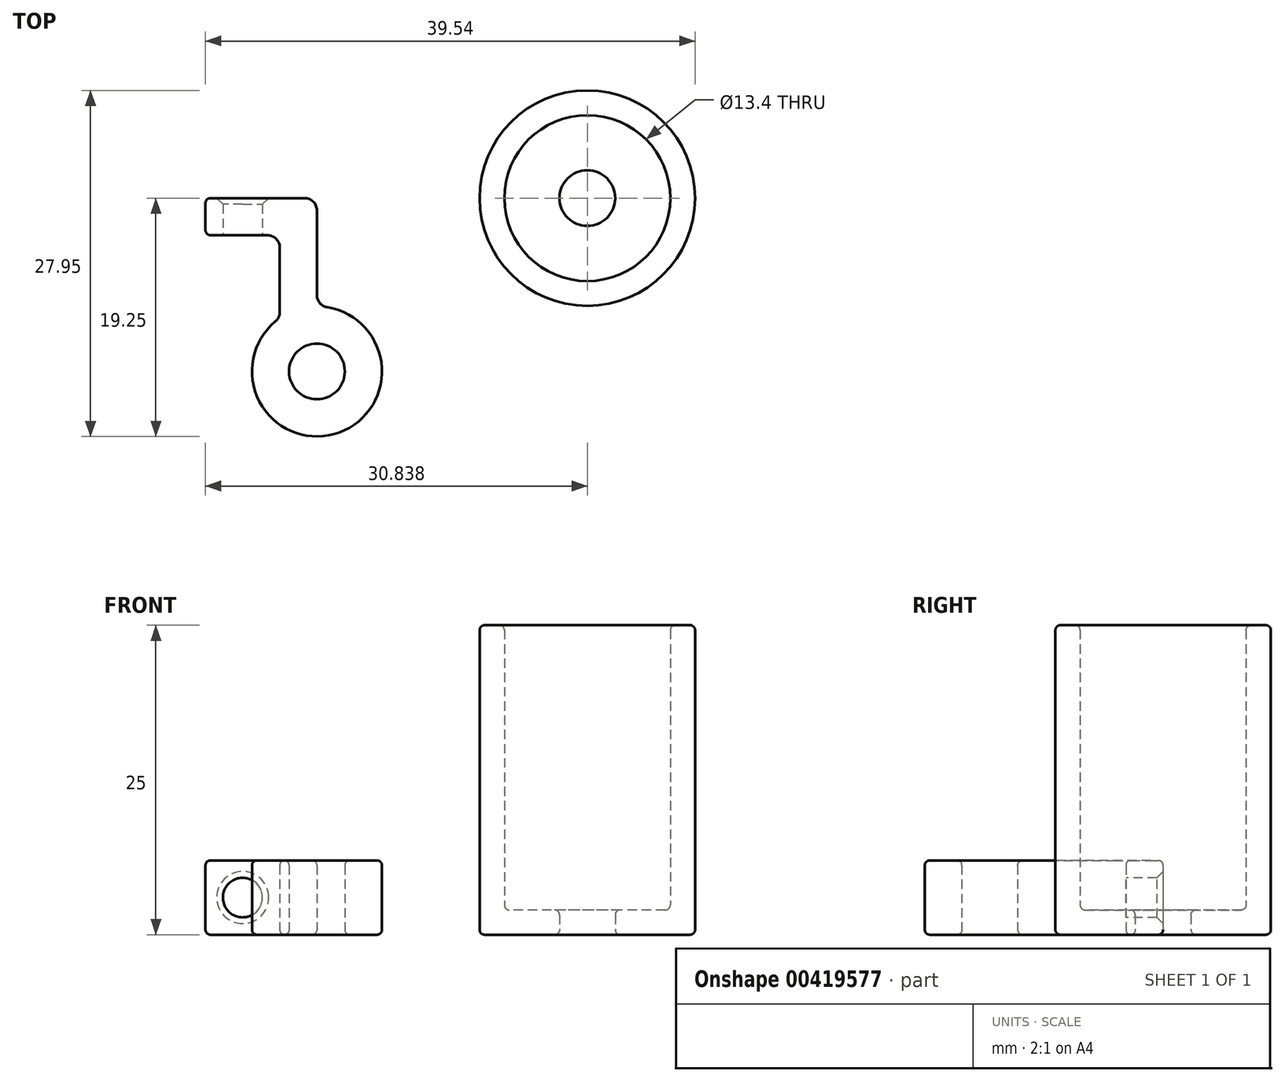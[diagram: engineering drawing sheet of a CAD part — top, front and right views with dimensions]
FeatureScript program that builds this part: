
annotation { "Feature Type Name" : "Feature", "Feature Type Description" : "" }
export const myFeature = defineFeature(function(context is Context, id is Id, definition is map)
    precondition{}
    {
        {
            var Q0;
            Q0=qCreatedBy(makeId("Top.planeOp"),FACE);
            var sketch = newSketch(context, id + "F0", { "sketchPlane" : qUnion([Q0])});
            skLineSegment(sketch, "E0", {"start": v(0, 0) * mm, "end": v(9, 0) * mm});
            skLineSegment(sketch, "E1", {"start": v(9, 0) * mm, "end": v(9, -8.75) * mm});
            skLineSegment(sketch, "E2", {"start": v(9, -14) * mm, "end": v(6, -14) * mm, "construction": true});
            skLineSegment(sketch, "E3", {"start": v(6, -14) * mm, "end": v(6, -9.7) * mm, "construction": true});
            skLineSegment(sketch, "E4", {"start": v(6, -3) * mm, "end": v(0, -3) * mm});
            skLineSegment(sketch, "E5", {"start": v(0, -3) * mm, "end": v(0, 0) * mm});
            skPoint(sketch, "E6", {"position": v(3, -3) * mm});
            skCircle(sketch, "E7", {"center": v(30.84, 0) * mm, "radius": 8.7 * mm});
            skCircle(sketch, "E8", {"center": v(30.84, 0) * mm, "radius": 6.7 * mm});
            skCircle(sketch, "E9", {"center": v(30.84, 0) * mm, "radius": 2.25 * mm});
            skCircle(sketch, "E10", {"center": v(9, -14) * mm, "radius": 2.25 * mm});
            skLineSegment(sketch, "E11", {"start": v(9, -11.75) * mm, "end": v(9, -14) * mm, "construction": true});
            skLineSegment(sketch, "E12", {"start": v(6, -9.7) * mm, "end": v(6, -3) * mm});
            skLineSegment(sketch, "E13", {"start": v(9, -8.75) * mm, "end": v(9, -11.75) * mm, "construction": true});
            skArc(sketch, "E14", {"start": v(6, -9.7) * mm, "mid": v(10.57, -19) * mm, "end": v(9, -8.75) * mm});
            skArc(sketch, "E15", {"start": v(9, -8.75) * mm, "mid": v(7.43, -9) * mm, "end": v(6, -9.7) * mm, "construction": true});
            skSolve(sketch);
        }
        {
            var Q0;
            Q0=makeQuery(id+"F0.imprint","IMPRINT",FACE,{"disambiguationData":[TD([[makeQuery(id+"F0.imprint","IMPRINT",EDGE,{"derivedFrom":sQuery(id+"F0.wireOp",EDGE,"E0")}),-1.0]])]});
            extrude(context, id + "F1", {"entities" : qUnion([Q0]), "depth" : 6 * mm});
        }
        {
            var Q0;
            Q0=makeQuery(id+"F1.opExtrude","SWEPT_FACE",FACE,{"disambiguationData":[OSD([sQuery(id+"F0.wireOp",EDGE,"E4")])]});
            var sketch = newSketch(context, id + "F2", { "sketchPlane" : qUnion([Q0])});
            skPoint(sketch, "E16.0", {"position": v(3, 6) * mm});
            skPoint(sketch, "E16.1", {"position": v(0, 3) * mm});
            skCircle(sketch, "E17", {"center": v(3, 3) * mm, "radius": 1.6 * mm});
            skSolve(sketch);
        }
        {
            var Q0;
            Q0=makeQuery(id+"F2.imprint","IMPRINT",FACE,{"disambiguationData":[TD([[makeQuery(id+"F2.imprint","IMPRINT",EDGE,{"derivedFrom":sQuery(id+"F2.wireOp",EDGE,"E17")}),1.0]])]});
            extrude(context, id + "F3", {"entities" : qUnion([Q0]), "operationType" : NewBodyOperationType.REMOVE, "endBound" : BoundingType.THROUGH_ALL, "oppositeDirection" : true, "depth" : 25 * mm});
        }
        {
            var Q0;
            Q0=makeQuery(id+"F3.boolean.opBoolean","COPY",EDGE,{"derivedFrom":makeQuery(id+"F3.opExtrude","CAP_EDGE",EDGE,{"disambiguationData":[OSD([sQuery(id+"F2.wireOp",EDGE,"E17")])],"isStart":true})});
            var Q1;
            Q1=makeQuery(id+"F3.boolean.opBoolean","INTERSECT",EDGE,{"derivedFrom":[makeQuery(id+"F1.opExtrude","SWEPT_FACE",FACE,{"disambiguationData":[OSD([sQuery(id+"F0.wireOp",EDGE,"E0")])]}),makeQuery(id+"F3.opExtrude","SWEPT_FACE",FACE,{"disambiguationData":[OSD([sQuery(id+"F2.wireOp",EDGE,"E17")])]})]});
            chamfer(context, id + "F4", {"entities" : qUnion([Q0, Q1]), "width" : 0.5 * mm, "tangentPropagation" : true});
        }
        {
            var Q0;
            Q0=makeQuery(id+"F1.opExtrude","SWEPT_EDGE",EDGE,{"disambiguationData":[OSD([sQuery(id+"F0.wireOp",EDGE,"E4"),sQuery(id+"F0.wireOp",EDGE,"E12")])]});
            var Q1;
            Q1=makeQuery(id+"F1.opExtrude","SWEPT_EDGE",EDGE,{"disambiguationData":[OSD([sQuery(id+"F0.wireOp",EDGE,"E0"),sQuery(id+"F0.wireOp",EDGE,"E1")])]});
            var Q2;
            Q2=makeQuery(id+"F1.opExtrude","SWEPT_EDGE",EDGE,{"disambiguationData":[OSD([sQuery(id+"F0.wireOp",EDGE,"E0"),sQuery(id+"F0.wireOp",EDGE,"E1")])]});
            var Q3;
            Q3=makeQuery(id+"F1.opExtrude","SWEPT_EDGE",EDGE,{"disambiguationData":[OSD([sQuery(id+"F0.wireOp",EDGE,"E1"),sQuery(id+"F0.wireOp",EDGE,"E14")])]});
            var Q4;
            Q4=makeQuery(id+"F1.opExtrude","SWEPT_EDGE",EDGE,{"disambiguationData":[OSD([sQuery(id+"F0.wireOp",EDGE,"E12"),sQuery(id+"F0.wireOp",EDGE,"E14")])]});
            fillet(context, id + "F5", {"entities" : qUnion([Q0, Q1, Q2, Q3, Q4]), "radius" : 1 * mm, "tangentPropagation" : true, "allowEdgeOverflow" : false});
        }
        {
            var Q0;
            Q0=makeQuery(id+"F1.opExtrude","CAP_FACE",FACE,{"disambiguationData":[OSD([sQuery(id+"F0.wireOp",EDGE,"E0"),sQuery(id+"F0.wireOp",EDGE,"E1"),sQuery(id+"F0.wireOp",EDGE,"E3"),sQuery(id+"F0.wireOp",EDGE,"E4"),sQuery(id+"F0.wireOp",EDGE,"E5"),sQuery(id+"F0.wireOp",EDGE,"hKZQIiYS-rxz7-eE48-JcK7-Gq0U2qqFNY88"),sQuery(id+"F0.wireOp",EDGE,"jA0uWVU0-jQQE-gLF9-S8yV-XQNs91lV4omb"),sQuery(id+"F0.wireOp",EDGE,"JiTG1y3F-Bukr-wDQm-vMhE-ftvG4FGmfDrU"),sQuery(id+"F0.wireOp",EDGE,"ydXRLY5Y-or6F-EQnL-fuEy-0NgZuJFtCCgJ"),sQuery(id+"F0.wireOp",EDGE,"N8syyVMO-PUAH-mnqF-dZnC-whcbOHcJgOkJ"),sQuery(id+"F0.wireOp",EDGE,"078516ff-2ed3-4372-9200-a547c36167fe0.MirrorCS"),sQuery(id+"F0.wireOp",EDGE,"078516ff-2ed3-4372-9200-a547c36167fe1.MirrorCS"),sQuery(id+"F0.wireOp",EDGE,"078516ff-2ed3-4372-9200-a547c36167fe2.MirrorCS"),sQuery(id+"F0.wireOp",EDGE,"63117e65-028f-4ed6-ad80-138359c89662")])],"isStart":false});
            var Q1;
            Q1=makeQuery(id+"F1.opExtrude","CAP_FACE",FACE,{"disambiguationData":[OSD([sQuery(id+"F0.wireOp",EDGE,"E0"),sQuery(id+"F0.wireOp",EDGE,"E1"),sQuery(id+"F0.wireOp",EDGE,"E3"),sQuery(id+"F0.wireOp",EDGE,"E4"),sQuery(id+"F0.wireOp",EDGE,"E5"),sQuery(id+"F0.wireOp",EDGE,"hKZQIiYS-rxz7-eE48-JcK7-Gq0U2qqFNY88"),sQuery(id+"F0.wireOp",EDGE,"jA0uWVU0-jQQE-gLF9-S8yV-XQNs91lV4omb"),sQuery(id+"F0.wireOp",EDGE,"JiTG1y3F-Bukr-wDQm-vMhE-ftvG4FGmfDrU"),sQuery(id+"F0.wireOp",EDGE,"ydXRLY5Y-or6F-EQnL-fuEy-0NgZuJFtCCgJ"),sQuery(id+"F0.wireOp",EDGE,"N8syyVMO-PUAH-mnqF-dZnC-whcbOHcJgOkJ"),sQuery(id+"F0.wireOp",EDGE,"078516ff-2ed3-4372-9200-a547c36167fe0.MirrorCS"),sQuery(id+"F0.wireOp",EDGE,"078516ff-2ed3-4372-9200-a547c36167fe1.MirrorCS"),sQuery(id+"F0.wireOp",EDGE,"078516ff-2ed3-4372-9200-a547c36167fe2.MirrorCS"),sQuery(id+"F0.wireOp",EDGE,"63117e65-028f-4ed6-ad80-138359c89662")])],"isStart":true});
            var Q2;
            Q2=makeQuery(id+"F1.opExtrude","SWEPT_FACE",FACE,{"disambiguationData":[OSD([sQuery(id+"F0.wireOp",EDGE,"078516ff-2ed3-4372-9200-a547c36167fe0.MirrorCS")])]});
            var Q3;
            Q3=makeQuery(id+"F1.opExtrude","SWEPT_FACE",FACE,{"disambiguationData":[OSD([sQuery(id+"F0.wireOp",EDGE,"N8syyVMO-PUAH-mnqF-dZnC-whcbOHcJgOkJ")])]});
            var Q4;
            Q4=makeQuery(id+"F1.opExtrude","SWEPT_FACE",FACE,{"disambiguationData":[OSD([sQuery(id+"F0.wireOp",EDGE,"E5")])]});
            fillet(context, id + "F6", {"entities" : qUnion([Q0, Q1, Q2, Q3, Q4]), "radius" : 0.4 * mm, "tangentPropagation" : true, "allowEdgeOverflow" : false});
        }
        {
            var Q0;
            Q0=makeQuery(id+"F0.imprint","IMPRINT",FACE,{"disambiguationData":[TD([[makeQuery(id+"F0.imprint","IMPRINT",EDGE,{"derivedFrom":sQuery(id+"F0.wireOp",EDGE,"E7")}),1.0]])]});
            extrude(context, id + "F7", {"entities" : qUnion([Q0]), "depth" : 25 * mm});
        }
        {
            var Q0;
            Q0=makeQuery(id+"F0.imprint","IMPRINT",FACE,{"disambiguationData":[TD([[makeQuery(id+"F0.imprint","IMPRINT",EDGE,{"derivedFrom":sQuery(id+"F0.wireOp",EDGE,"E8")}),1.0]])]});
            extrude(context, id + "F8", {"entities" : qUnion([Q0]), "operationType" : NewBodyOperationType.ADD, "depth" : 2 * mm});
        }
        {
            var Q0;
            {var subQ0=sQuery(id+"F0.wireOp",EDGE,"E8");Q0=makeQuery(id+"F8.boolean.opBoolean","MERGE",FACE,{"derivedFrom":[makeQuery(id+"F7.opExtrude","CAP_FACE",FACE,{"disambiguationData":[OSD([sQuery(id+"F0.wireOp",EDGE,"E7"),subQ0])],"isStart":true}),makeQuery(id+"F8.opExtrude","CAP_FACE",FACE,{"disambiguationData":[OSD([subQ0,sQuery(id+"F0.wireOp",EDGE,"E9")])],"isStart":true})]});}
            var Q1;
            Q1=makeQuery(id+"F8.opExtrude","CAP_FACE",FACE,{"disambiguationData":[OSD([sQuery(id+"F0.wireOp",EDGE,"E8"),sQuery(id+"F0.wireOp",EDGE,"E9")])],"isStart":false});
            var Q2;
            Q2=makeQuery(id+"F7.opExtrude","CAP_FACE",FACE,{"disambiguationData":[OSD([sQuery(id+"F0.wireOp",EDGE,"E7"),sQuery(id+"F0.wireOp",EDGE,"E8")])],"isStart":false});
            fillet(context, id + "F9", {"entities" : qUnion([Q0, Q1, Q2]), "radius" : 0.4 * mm, "tangentPropagation" : true, "allowEdgeOverflow" : false});
        }
    });
